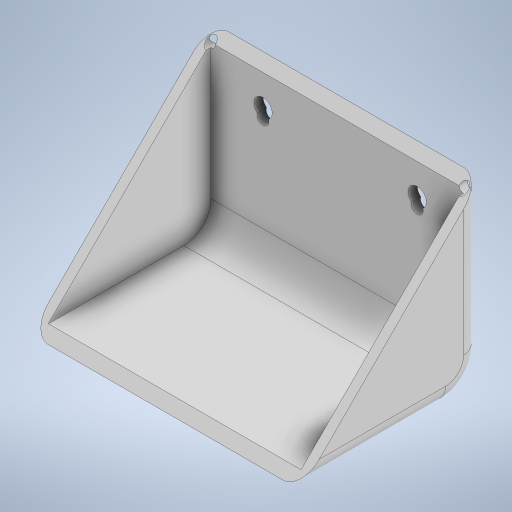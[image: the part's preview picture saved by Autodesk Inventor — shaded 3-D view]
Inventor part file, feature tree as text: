
AUTODESK INVENTOR PART (.ipt)
format: ipt  version: 2023 (Build 270158000, 158)  size: 276,992 bytes
history: native  units: in
note: dims shown in document units (in); Inventor stores cm internally (conversion verified against a paired STEP export)
features: sketch x5, extrude x4, fillet x2, shell x1, hole x1
ambient origin geometry x8: Origin, YZ Plane, XZ Plane, XY Plane, X Axis, Y Axis, Z Axis, Center Point
bodies: Solid1 (feature_tree)
feature tree (13):
  extrude  "Extrusion1"  Depth=5.0in
  fillet  "Fillet1"  Radius=7.5in
  shell  "Shell1"  Thickness=1.0in
  fillet  "Fillet2"  Radius=0.25in
  extrude  "Extrusion2"  Depth=0.25in
  extrude  "Extrusion3"  Depth=1.0in TaperAngle=0.0deg
  extrude  "Extrusion4"  Depth=0.5in
  hole  "Hole1"  [1 undecoded]
  sketch  "Sketch1"  dims[d0=5.0in d1=5.0in d2=7.5in d3=0.0in d4=1.0in d5=0.25in]
  sketch  "Sketch2"  dims[d6=0.5in d7=0.25in]
  sketch  "Sketch3"  dims[d8=2.5in d9=1.0in d10=0.0in]
  sketch  "Sketch4"  dims[d11=0.5in d12=0.5in]
  sketch  "Sketch5"  dims[d13=1.0in d14=0.0in d15=0.325in d16=0.325in d17=1.0in d18=0.0in d19=0.25in d20=0.75in d21=0.375in d22=0.25in d23=0.5635in d24=1.0in d25=0.8108in]
note: 1 required parameter value undecoded (feature->parameter linkage not recoverable at this tier; creation-order binding heuristic only, values carry confidence <= 0.55)
